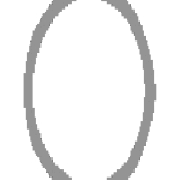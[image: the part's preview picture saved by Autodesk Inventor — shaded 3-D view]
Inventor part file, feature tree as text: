
AUTODESK INVENTOR PART (.ipt)
format: ipt  version: 2021 (Build 250183000, 183)  size: 109,568 bytes
history: native  units: in
note: dims shown in document units (in); Inventor stores cm internally (conversion verified against a paired STEP export)
features: other x4, sketch x3, plane x1
ambient origin geometry x8: Origin, YZ Plane, XZ Plane, XY Plane, X Axis, Y Axis, Z Axis, Center Point
bodies: Solid1 (feature_tree), Body (feature_tree)
feature tree (8):
  other  "Driven Length"
  other  "Frame Generator"
  other  "Start Plane"
  other  "End Plane"
  sketch  "Sketch"  dims[d2=15.625in d4=-0.0in d5=15.625in d6=0.12in d7=0.0in d8=90.0deg d9=15.625in]
  sketch  "Sketch2"  dims[d0=1.0in]
  plane  "Work Plane3"
  sketch  "Sketch3"  dims[d1=0.065in]
